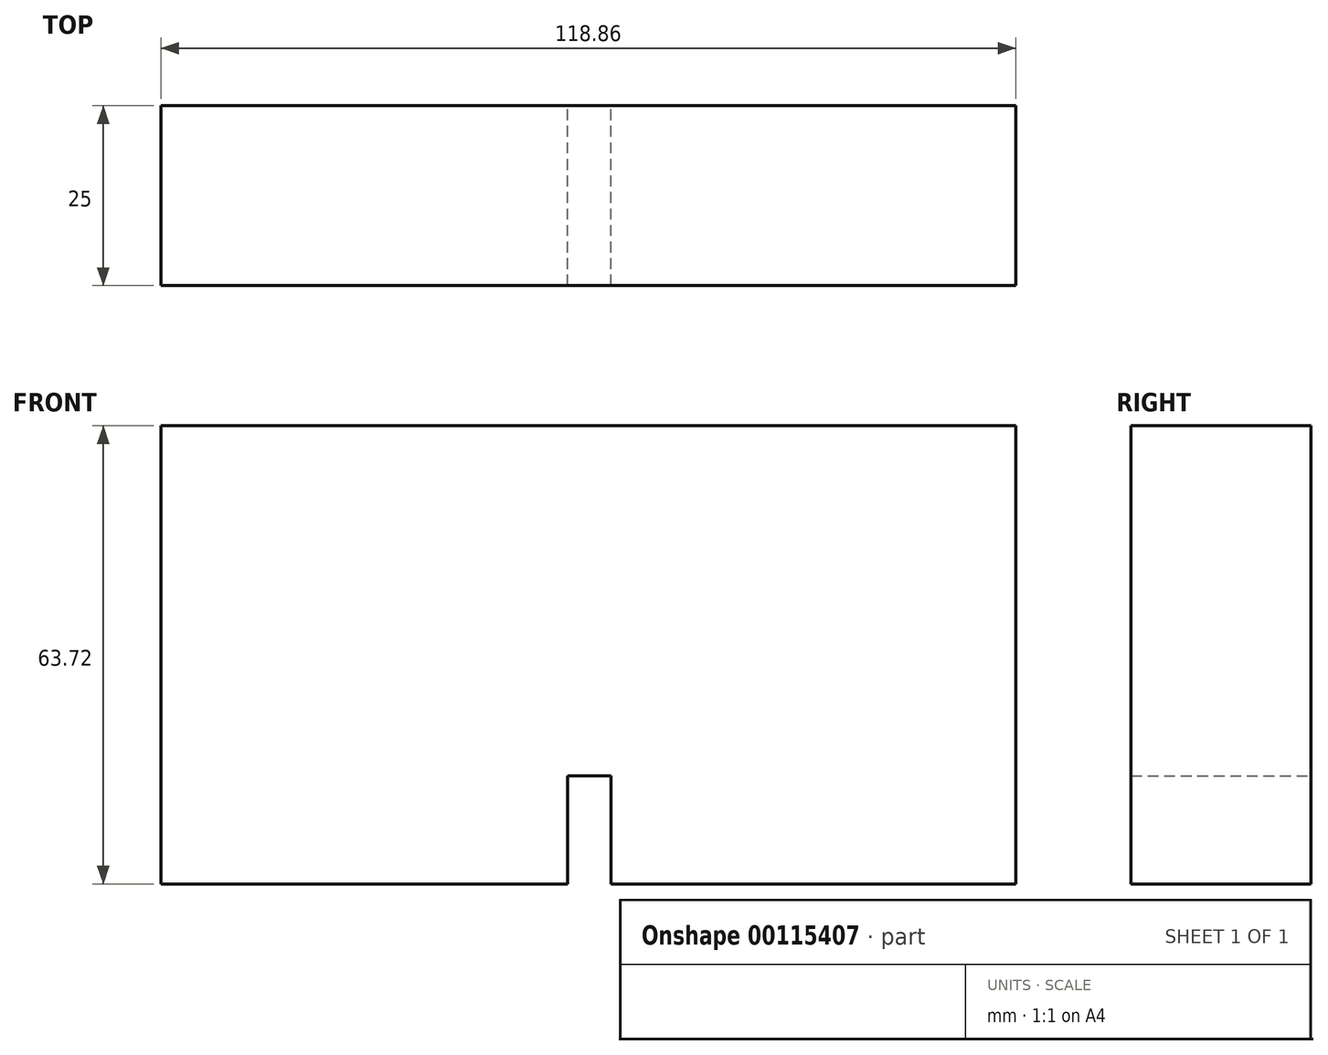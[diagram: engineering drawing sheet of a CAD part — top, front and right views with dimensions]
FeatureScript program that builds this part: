
annotation { "Feature Type Name" : "Feature", "Feature Type Description" : "" }
export const myFeature = defineFeature(function(context is Context, id is Id, definition is map)
    precondition{}
    {
        {
            var Q0;
            Q0=qCreatedBy(makeId("Front.planeOp"),FACE);
            var sketch = newSketch(context, id + "F0", { "sketchPlane" : qUnion([Q0])});
            skLineSegment(sketch, "E0.bottom", {"start": v(59.43, -31.86) * mm, "end": v(3.14, -31.86) * mm});
            skLineSegment(sketch, "E0.top", {"start": v(59.43, 31.86) * mm, "end": v(-59.43, 31.86) * mm});
            skLineSegment(sketch, "E0.left", {"start": v(59.43, -31.86) * mm, "end": v(59.43, 31.86) * mm});
            skLineSegment(sketch, "E0.right", {"start": v(-59.43, -31.86) * mm, "end": v(-59.43, 31.86) * mm});
            skPoint(sketch, "E0.middle", {"position": v(0, 0) * mm});
            skLineSegment(sketch, "E1.top", {"start": v(-2.86, -16.86) * mm, "end": v(3.14, -16.86) * mm});
            skLineSegment(sketch, "E1.left", {"start": v(-2.86, -31.86) * mm, "end": v(-2.86, -16.86) * mm});
            skLineSegment(sketch, "E1.right", {"start": v(3.14, -31.86) * mm, "end": v(3.14, -16.86) * mm});
            skLineSegment(sketch, "E2.trimOffspring", {"start": v(-2.86, -31.86) * mm, "end": v(-59.43, -31.86) * mm});
            skSolve(sketch);
        }
        {
            var Q0;
            Q0 = qSketchRegion(id + "F0", true);
            extrude(context, id + "F1", {"entities" : qUnion([Q0]), "depth" : 25 * mm});
        }
    });
